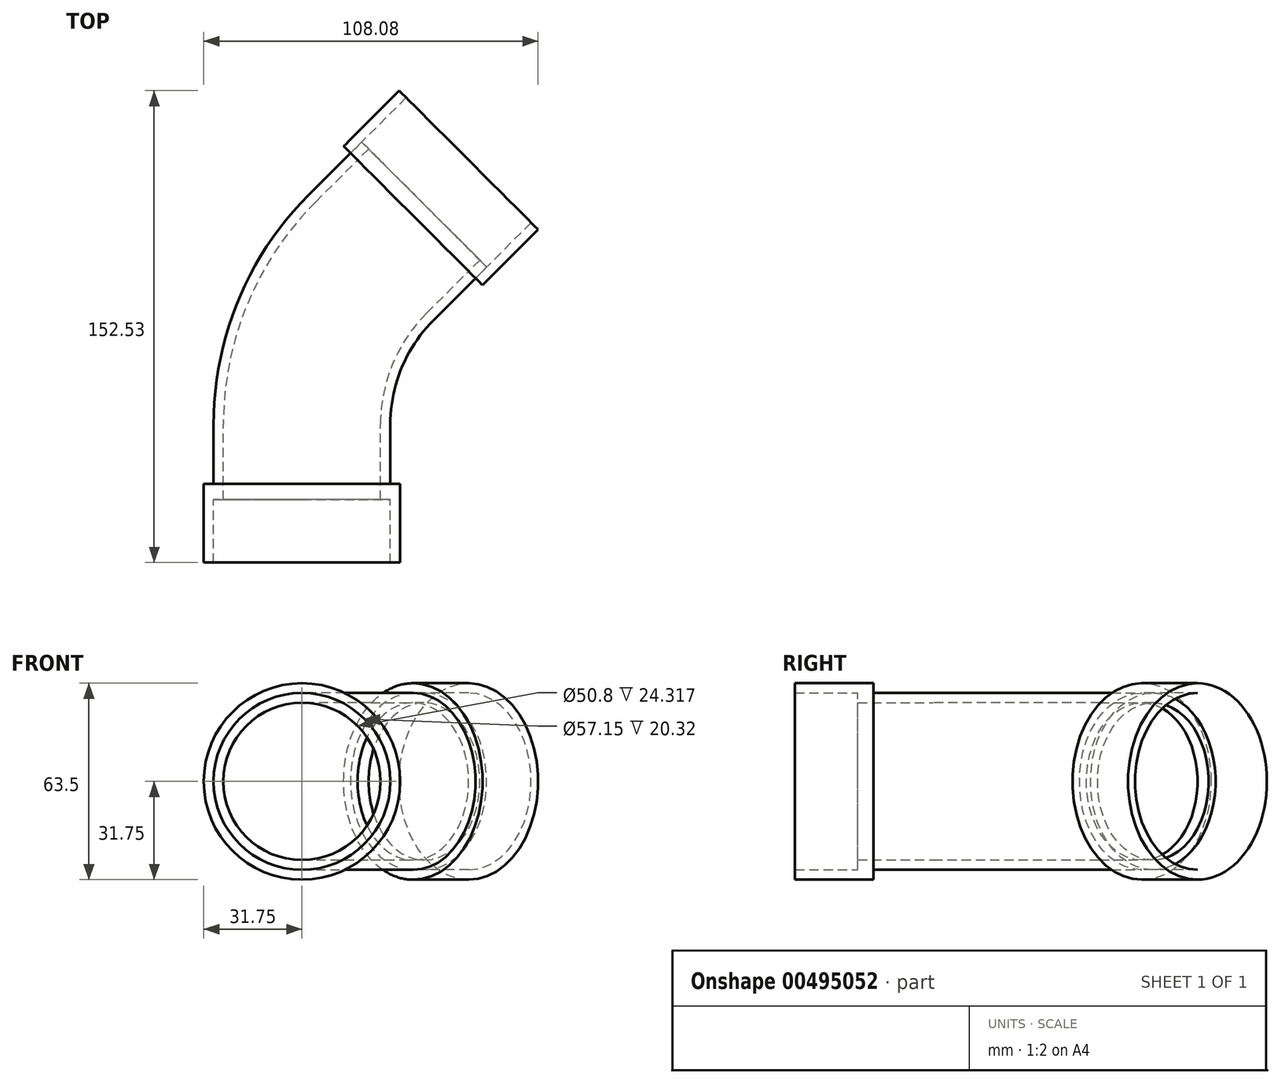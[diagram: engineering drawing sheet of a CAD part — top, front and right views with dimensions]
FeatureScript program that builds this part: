
annotation { "Feature Type Name" : "Feature", "Feature Type Description" : "" }
export const myFeature = defineFeature(function(context is Context, id is Id, definition is map)
    precondition{}
    {
        {
            var Q0;
            Q0=qCreatedBy(makeId("Front.planeOp"),FACE);
            var sketch = newSketch(context, id + "F0", { "sketchPlane" : qUnion([Q0])});
            skCircle(sketch, "E0", {"center": v(0, 0) * mm, "radius": 25.4 * mm});
            skCircle(sketch, "E1", {"center": v(0, 0) * mm, "radius": 28.58 * mm});
            skCircle(sketch, "E2", {"center": v(0, 0) * mm, "radius": 31.75 * mm});
            skSolve(sketch);
        }
        {
            var Q0;
            Q0=qCreatedBy(makeId("Top.planeOp"),FACE);
            var sketch = newSketch(context, id + "F1", { "sketchPlane" : qUnion([Q0])});
            skLineSegment(sketch, "E3", {"start": v(0, 0) * mm, "end": v(0, 19.24) * mm});
            skLineSegment(sketch, "E4.bottom", {"start": v(0, 50.8) * mm, "end": v(35.92, 50.8) * mm});
            skLineSegment(sketch, "E4.top", {"start": v(0, 86.72) * mm, "end": v(35.92, 86.72) * mm});
            skLineSegment(sketch, "E4.left", {"start": v(0, 50.8) * mm, "end": v(0, 86.72) * mm});
            skLineSegment(sketch, "E4.right", {"start": v(35.92, 50.8) * mm, "end": v(35.92, 86.72) * mm});
            skLineSegment(sketch, "E5", {"start": v(22.32, 73.12) * mm, "end": v(35.92, 86.72) * mm});
            skPoint(sketch, "E6.visualSharp", {"position": v(0, 50.8) * mm});
            skArc(sketch, "E6.filletArc", {"start": v(22.32, 73.12) * mm, "mid": v(5.8, 48.4) * mm, "end": v(0, 19.24) * mm});
            skSolve(sketch);
        }
        {
            var Q0;
            Q0=makeQuery(id+"F0.imprint","IMPRINT",FACE,{"disambiguationData":[TD([[makeQuery(id+"F0.imprint","IMPRINT",EDGE,{"derivedFrom":sQuery(id+"F0.wireOp",EDGE,"E0")}),-1.0]])]});
            var Q1;
            Q1=sQuery(id+"F1.wireOp",EDGE,"E3");
            var Q2;
            Q2=sQuery(id+"F1.wireOp",EDGE,"E6.filletArc");
            var Q3;
            Q3=sQuery(id+"F1.wireOp",EDGE,"E5");
            sweep(context, id + "F2", {"profiles" : qUnion([Q0]), "path" : qUnion([Q1, Q2, Q3])});
        }
        {
            var Q0;
            Q0=makeQuery(id+"F0.imprint","IMPRINT",FACE,{"disambiguationData":[TD([[makeQuery(id+"F0.imprint","IMPRINT",EDGE,{"derivedFrom":sQuery(id+"F0.wireOp",EDGE,"E0")}),-1.0]])]});
            extrude(context, id + "F3", {"entities" : qUnion([Q0]), "operationType" : NewBodyOperationType.ADD, "depth" : 5.08 * mm});
        }
        {
            var Q0;
            Q0=makeQuery(id+"F0.imprint","IMPRINT",FACE,{"disambiguationData":[TD([[makeQuery(id+"F0.imprint","IMPRINT",EDGE,{"derivedFrom":sQuery(id+"F0.wireOp",EDGE,"E1")}),-1.0]])]});
            var Q1;
            Q1=sQuery(id+"F0.wireOp",EDGE,"E2");
            extrude(context, id + "F4", {"entities" : qUnion([Q0]), "operationType" : NewBodyOperationType.ADD, "surfaceEntities" : qUnion([Q1]), "depth" : 25.4 * mm});
        }
        {
            var Q0;
            Q0=makeQuery(id+"F2.opSweep","CAP_FACE",FACE,{"disambiguationData":[OSD([sQuery(id+"F0.wireOp",EDGE,"E0"),sQuery(id+"F0.wireOp",EDGE,"E1"),sQuery(id+"F1.wireOp",VERTEX,"E5.end")])],"isStart":false});
            var sketch = newSketch(context, id + "F5", { "sketchPlane" : qUnion([Q0])});
            skCircle(sketch, "E7.0", {"center": v(35.92, 0) * mm, "radius": 25.4 * mm});
            skCircle(sketch, "E8.0", {"center": v(35.92, 0) * mm, "radius": 28.58 * mm});
            skCircle(sketch, "E9", {"center": v(35.92, 0) * mm, "radius": 31.75 * mm});
            skSolve(sketch);
        }
        {
            var Q0;
            Q0 = qSketchRegion(id + "F5", true);
            extrude(context, id + "F6", {"entities" : qUnion([Q0]), "depth" : 25.4 * mm});
        }
        {
            var Q0;
            Q0=makeQuery(id+"F2.opSweep","CAP_FACE",FACE,{"disambiguationData":[OSD([sQuery(id+"F0.wireOp",EDGE,"E0"),sQuery(id+"F0.wireOp",EDGE,"E1"),sQuery(id+"F1.wireOp",VERTEX,"E5.end")])],"isStart":false});
            extrude(context, id + "F7", {"entities" : qUnion([Q0]), "depth" : 5.08 * mm});
        }
    });
